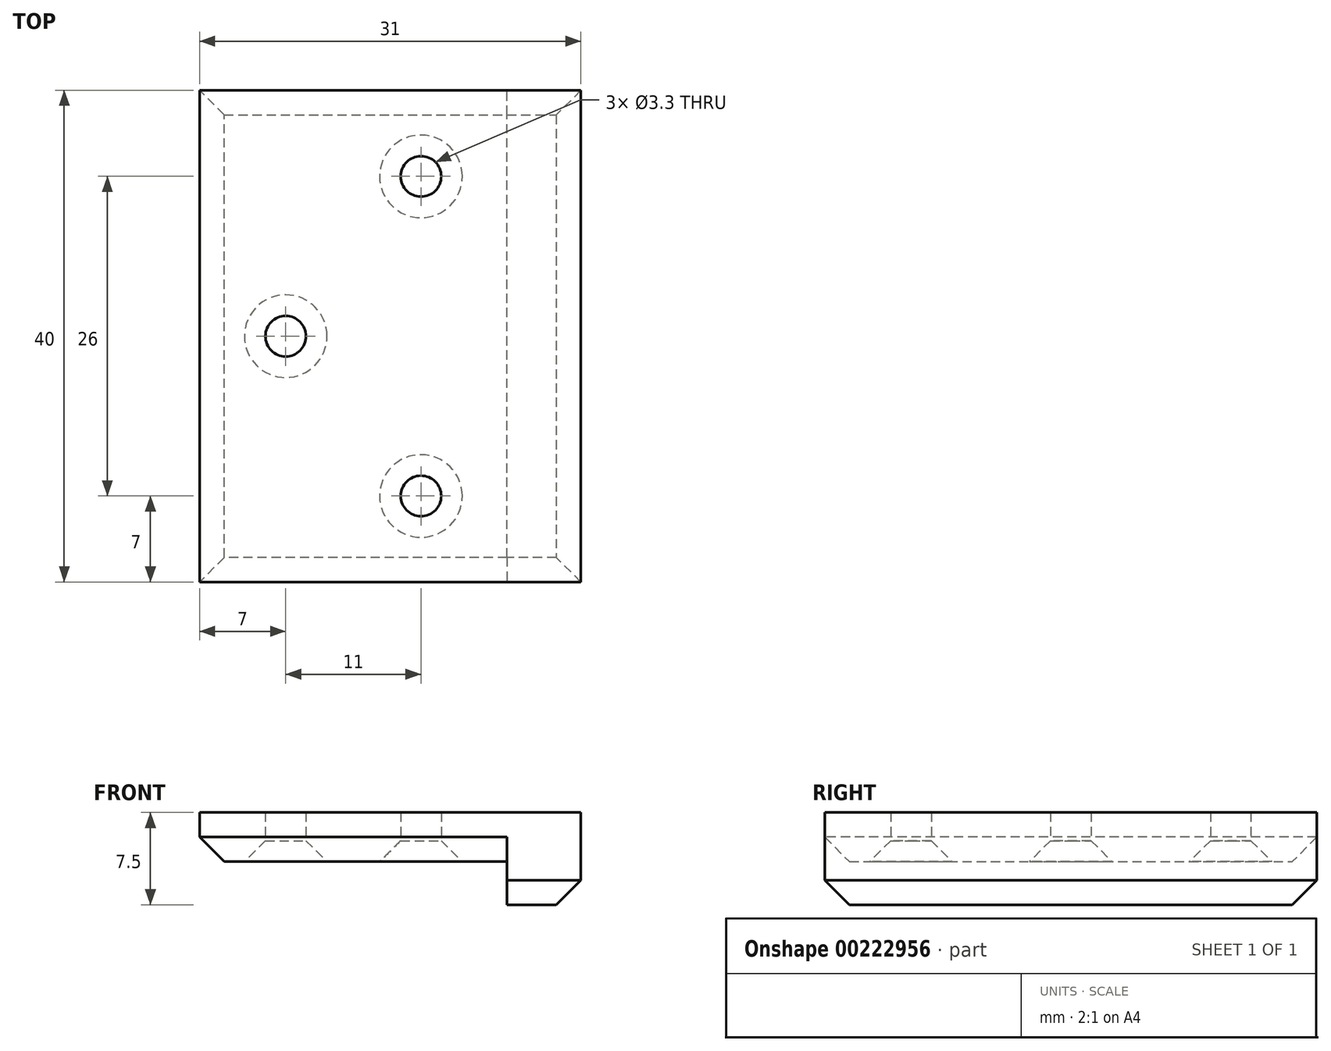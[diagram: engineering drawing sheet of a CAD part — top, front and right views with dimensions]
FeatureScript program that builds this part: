
annotation { "Feature Type Name" : "Feature", "Feature Type Description" : "" }
export const myFeature = defineFeature(function(context is Context, id is Id, definition is map)
    precondition{}
    {
        {
            var Q0;
            Q0=qCreatedBy(makeId("Front.planeOp"),FACE);
            var sketch = newSketch(context, id + "F0", { "sketchPlane" : qUnion([Q0])});
            skLineSegment(sketch, "E0", {"start": v(-31, 0) * mm, "end": v(-6, 0) * mm});
            skLineSegment(sketch, "E1", {"start": v(-6, 0) * mm, "end": v(-6, -3.5) * mm});
            skLineSegment(sketch, "E2", {"start": v(-6, -3.5) * mm, "end": v(0, -3.5) * mm});
            skLineSegment(sketch, "E3", {"start": v(0, -3.5) * mm, "end": v(0, 4) * mm});
            skLineSegment(sketch, "E4", {"start": v(0, 4) * mm, "end": v(-31, 4) * mm});
            skLineSegment(sketch, "E5", {"start": v(-31, 4) * mm, "end": v(-31, 0) * mm});
            skSolve(sketch);
        }
        {
            var Q0;
            Q0 = qSketchRegion(id + "F0", true);
            extrude(context, id + "F1", {"entities" : qUnion([Q0]), "endBound" : BoundingType.SYMMETRIC, "depth" : 40 * mm});
        }
        {
            var Q0;
            Q0=qCreatedBy(makeId("Top.planeOp"),FACE);
            var sketch = newSketch(context, id + "F2", { "sketchPlane" : qUnion([Q0])});
            skPoint(sketch, "E6", {"position": v(-24, 0) * mm});
            skPoint(sketch, "E7", {"position": v(-13, 13) * mm});
            skPoint(sketch, "E8", {"position": v(-13, -13) * mm});
            skSolve(sketch);
        }
        {
            var Q0;
            Q0=sQuery(id+"F2.wireOp",VERTEX,"E7");
            var Q1;
            Q1=sQuery(id+"F2.wireOp",VERTEX,"E6");
            var Q2;
            Q2=sQuery(id+"F2.wireOp",VERTEX,"E8");
            var Q3;
            Q3=makeQuery(id+"F1.opExtrude","SWEPT_BODY",BODY,{"disambiguationData":[OSD([sQuery(id+"F0.wireOp",EDGE,"E0"),sQuery(id+"F0.wireOp",EDGE,"E1"),sQuery(id+"F0.wireOp",EDGE,"E2"),sQuery(id+"F0.wireOp",EDGE,"E3"),sQuery(id+"F0.wireOp",EDGE,"E4"),sQuery(id+"F0.wireOp",EDGE,"E5")])]});
            hole(context, id + "F3", {"style" : HoleStyle.C_SINK, "endStyle" : HoleEndStyle.THROUGH, "oppositeDirection" : true, "standardTappedOrClearance" : lookupTablePath({ "standard" : "ISO", "fit" : "Normal", "size" : "M3", "type" : "Clearance" }), "standardBlindInLast" : lookupTablePath({ "fit" : "Standard", "standard" : "ISO", "size" : "M3", "type" : "Clearance" }), "holeDiameter" : 3.3 * mm, "cSinkDiameter" : 6.72 * mm, "cSinkAngle" : 90 * degree, "locations" : qUnion([Q0, Q1, Q2]), "scope" : qUnion([Q3]), "isTappedThrough" : true});
        }
        {
            var Q0;
            Q0=makeQuery(id+"F1.opExtrude","CAP_EDGE",EDGE,{"disambiguationData":[OSD([sQuery(id+"F0.wireOp",EDGE,"E0")])],"isStart":false});
            var Q1;
            Q1=makeQuery(id+"F1.opExtrude","SWEPT_EDGE",EDGE,{"disambiguationData":[OSD([sQuery(id+"F0.wireOp",EDGE,"E0"),sQuery(id+"F0.wireOp",EDGE,"E5")])]});
            var Q2;
            Q2=makeQuery(id+"F1.opExtrude","CAP_EDGE",EDGE,{"disambiguationData":[OSD([sQuery(id+"F0.wireOp",EDGE,"E0")])],"isStart":true});
            var Q3;
            Q3=makeQuery(id+"F1.opExtrude","CAP_EDGE",EDGE,{"disambiguationData":[OSD([sQuery(id+"F0.wireOp",EDGE,"E2")])],"isStart":false});
            var Q4;
            Q4=makeQuery(id+"F1.opExtrude","CAP_EDGE",EDGE,{"disambiguationData":[OSD([sQuery(id+"F0.wireOp",EDGE,"E2")])],"isStart":true});
            var Q5;
            Q5=makeQuery(id+"F1.opExtrude","SWEPT_EDGE",EDGE,{"disambiguationData":[OSD([sQuery(id+"F0.wireOp",EDGE,"E2"),sQuery(id+"F0.wireOp",EDGE,"E3")])]});
            chamfer(context, id + "F4", {"entities" : qUnion([Q0, Q1, Q2, Q3, Q4, Q5]), "width" : 2 * mm, "tangentPropagation" : true});
        }
    });
